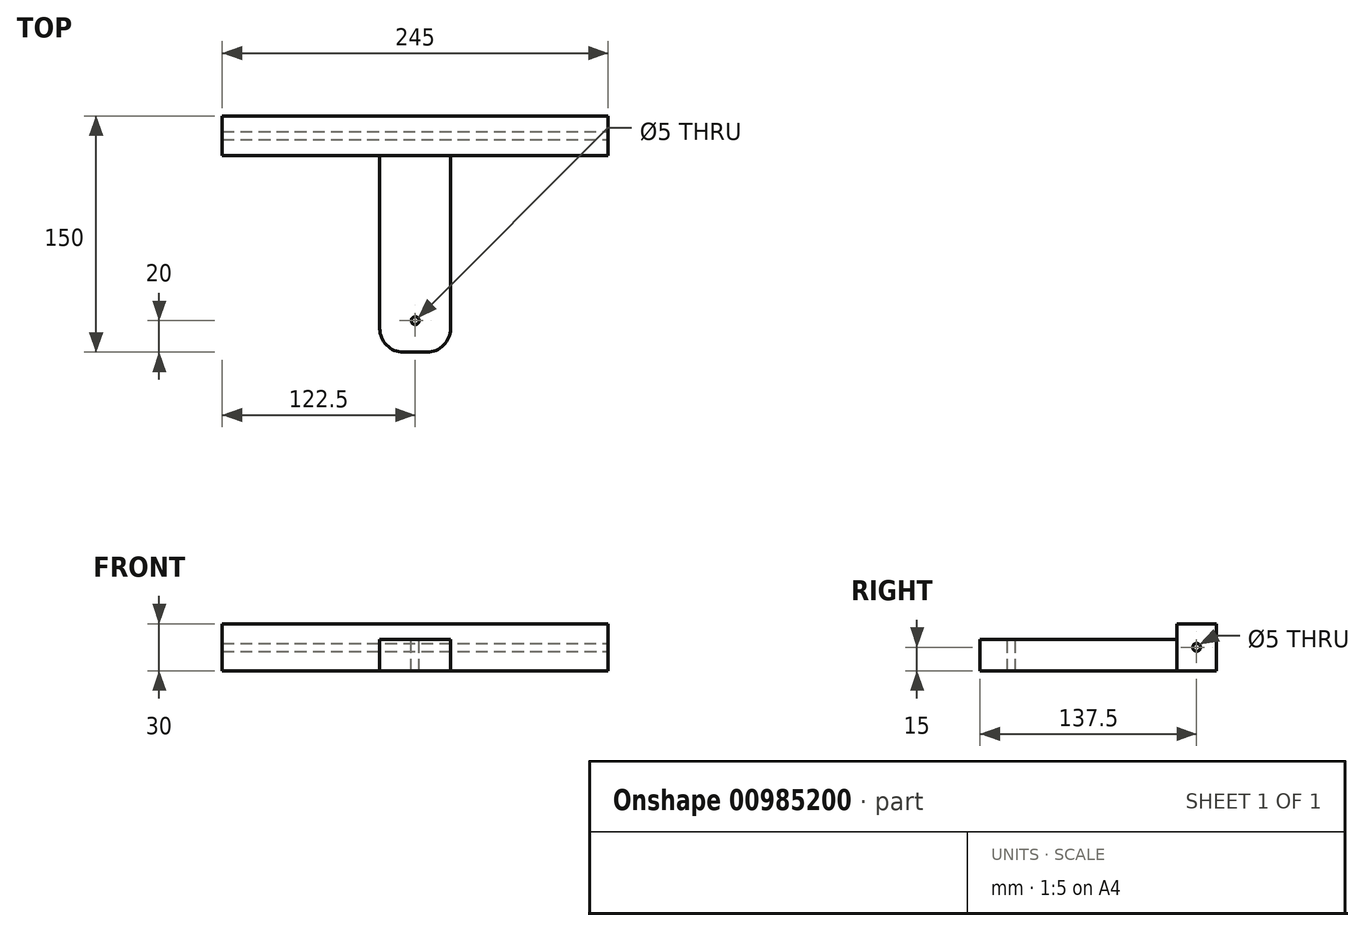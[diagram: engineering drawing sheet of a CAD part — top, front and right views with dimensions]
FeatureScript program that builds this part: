
annotation { "Feature Type Name" : "Feature", "Feature Type Description" : "" }
export const myFeature = defineFeature(function(context is Context, id is Id, definition is map)
    precondition{}
    {
        {
            var Q0;
            Q0=qCreatedBy(makeId("Front.planeOp"),FACE);
            var sketch = newSketch(context, id + "F0", { "sketchPlane" : qUnion([Q0])});
            skLineSegment(sketch, "E0.top", {"start": v(0, -20) * mm, "end": v(-22.5, -20) * mm});
            skLineSegment(sketch, "E0.right", {"start": v(-22.5, -30) * mm, "end": v(-22.5, -20) * mm});
            skLineSegment(sketch, "E1.bottom", {"start": v(-22.5, -30) * mm, "end": v(-122.5, -30) * mm});
            skLineSegment(sketch, "E1.top", {"start": v(0, 0) * mm, "end": v(-122.5, 0) * mm});
            skLineSegment(sketch, "E1.left", {"start": v(0, -20) * mm, "end": v(0, 0) * mm});
            skLineSegment(sketch, "E1.right", {"start": v(-122.5, -30) * mm, "end": v(-122.5, 0) * mm});
            skLineSegment(sketch, "E2.MirrorCS", {"start": v(0, 0) * mm, "end": v(122.5, 0) * mm});
            skLineSegment(sketch, "E3.MirrorCS", {"start": v(122.5, -30) * mm, "end": v(122.5, 0) * mm});
            skLineSegment(sketch, "E4.MirrorCS", {"start": v(0, -20) * mm, "end": v(22.5, -20) * mm});
            skLineSegment(sketch, "E5.MirrorCS", {"start": v(22.5, -30) * mm, "end": v(122.5, -30) * mm});
            skLineSegment(sketch, "E6.MirrorCS", {"start": v(22.5, -30) * mm, "end": v(22.5, -20) * mm});
            skSolve(sketch);
        }
        {
            var Q0;
            Q0 = qSketchRegion(id + "F0", true);
            extrude(context, id + "F1", {"entities" : qUnion([Q0]), "depth" : 25 * mm, "offsetDistance" : 25 * mm});
        }
        {
            var Q0;
            Q0=qCreatedBy(makeId("Right.planeOp"),FACE);
            var sketch = newSketch(context, id + "F2", { "sketchPlane" : qUnion([Q0])});
            skLineSegment(sketch, "E7", {"start": v(-150, -10) * mm, "end": v(-25, -10) * mm});
            skLineSegment(sketch, "E8", {"start": v(-25, -10) * mm, "end": v(-25, -20) * mm});
            skLineSegment(sketch, "E9", {"start": v(-25, -20) * mm, "end": v(0, -20) * mm});
            skLineSegment(sketch, "E10", {"start": v(0, -20) * mm, "end": v(0, -30) * mm});
            skLineSegment(sketch, "E11", {"start": v(0, -30) * mm, "end": v(-150, -30) * mm});
            skLineSegment(sketch, "E12", {"start": v(-150, -30) * mm, "end": v(-150, -10) * mm});
            skPoint(sketch, "E13", {"position": v(-12.5, -15) * mm});
            skPoint(sketch, "E13.positionSnap0", {"position": v(-12.5, -20) * mm});
            skSolve(sketch);
        }
        {
            var Q0;
            Q0 = qSketchRegion(id + "F2", true);
            extrude(context, id + "F3", {"entities" : qUnion([Q0]), "operationType" : NewBodyOperationType.ADD, "depth" : 22.5 * mm, "offsetDistance" : 25 * mm, "hasSecondDirection" : true, "secondDirectionOppositeDirection" : true, "secondDirectionDepth" : 22.5 * mm});
        }
        {
            var Q0;
            Q0=makeQuery(id+"F3.opExtrude","CAP_EDGE",EDGE,{"disambiguationData":[OSD([sQuery(id+"F2.wireOp",EDGE,"E12")])],"isStart":true});
            var Q1;
            Q1=makeQuery(id+"F3.opExtrude","CAP_EDGE",EDGE,{"disambiguationData":[OSD([sQuery(id+"F2.wireOp",EDGE,"E12")])],"isStart":false});
            fillet(context, id + "F4", {"entities" : qUnion([Q0, Q1]), "tangentPropagation" : true, "radius" : 15 * mm, "defaultsChanged" : true, "vertexSettings" : [], "allowEdgeOverflow" : false});
        }
        {
            var Q0;
            Q0=qCreatedBy(makeId("Top.planeOp"),FACE);
            var sketch = newSketch(context, id + "F5", { "sketchPlane" : qUnion([Q0])});
            skCircle(sketch, "E14", {"center": v(0, -130) * mm, "radius": 1.3 * mm});
            skSolve(sketch);
        }
        {
            var Q0;
            Q0=sQuery(id+"F5.wireOp",VERTEX,"E14.center");
            var Q1;
            Q1=makeQuery(id+"F1.opExtrude","SWEPT_BODY",BODY,{"disambiguationData":[OSD([sQuery(id+"F0.wireOp",EDGE,"E0.top"),sQuery(id+"F0.wireOp",EDGE,"E0.right"),sQuery(id+"F0.wireOp",EDGE,"E1.bottom"),sQuery(id+"F0.wireOp",EDGE,"E1.top"),sQuery(id+"F0.wireOp",EDGE,"E1.right"),sQuery(id+"F0.wireOp",EDGE,"E2.MirrorCS"),sQuery(id+"F0.wireOp",EDGE,"E3.MirrorCS"),sQuery(id+"F0.wireOp",EDGE,"E4.MirrorCS"),sQuery(id+"F0.wireOp",EDGE,"E5.MirrorCS"),sQuery(id+"F0.wireOp",EDGE,"E6.MirrorCS")])]});
            hole(context, id + "F6", {"style" : HoleStyle.SIMPLE, "endStyle" : HoleEndStyle.THROUGH, "holeDiameter" : 5 * mm, "majorDiameter" : 5 * mm, "isTappedThrough" : true, "tappedDepth" : 12 * mm, "tapClearance" : 3, "locations" : qUnion([Q0]), "scope" : qUnion([Q1])});
        }
        {
            var Q0;
            Q0=makeQuery(id+"F1.opExtrude","SWEPT_FACE",FACE,{"disambiguationData":[OSD([sQuery(id+"F0.wireOp",EDGE,"E3.MirrorCS")])]});
            var sketch = newSketch(context, id + "F7", { "sketchPlane" : qUnion([Q0])});
            skPoint(sketch, "E15", {"position": v(-12.5, -15) * mm});
            skSolve(sketch);
        }
        {
            var Q0;
            Q0=sQuery(id+"F7.wireOp",VERTEX,"E15");
            var Q1;
            Q1=makeQuery(id+"F1.opExtrude","SWEPT_BODY",BODY,{"disambiguationData":[OSD([sQuery(id+"F0.wireOp",EDGE,"E0.top"),sQuery(id+"F0.wireOp",EDGE,"E0.right"),sQuery(id+"F0.wireOp",EDGE,"E1.bottom"),sQuery(id+"F0.wireOp",EDGE,"E1.top"),sQuery(id+"F0.wireOp",EDGE,"E1.right"),sQuery(id+"F0.wireOp",EDGE,"E2.MirrorCS"),sQuery(id+"F0.wireOp",EDGE,"E3.MirrorCS"),sQuery(id+"F0.wireOp",EDGE,"E4.MirrorCS"),sQuery(id+"F0.wireOp",EDGE,"E5.MirrorCS"),sQuery(id+"F0.wireOp",EDGE,"E6.MirrorCS")])]});
            hole(context, id + "F8", {"style" : HoleStyle.SIMPLE, "endStyle" : HoleEndStyle.THROUGH, "holeDiameter" : 5 * mm, "majorDiameter" : 5 * mm, "isTappedThrough" : true, "tappedDepth" : 12 * mm, "tapClearance" : 3, "locations" : qUnion([Q0]), "scope" : qUnion([Q1])});
        }
    });
